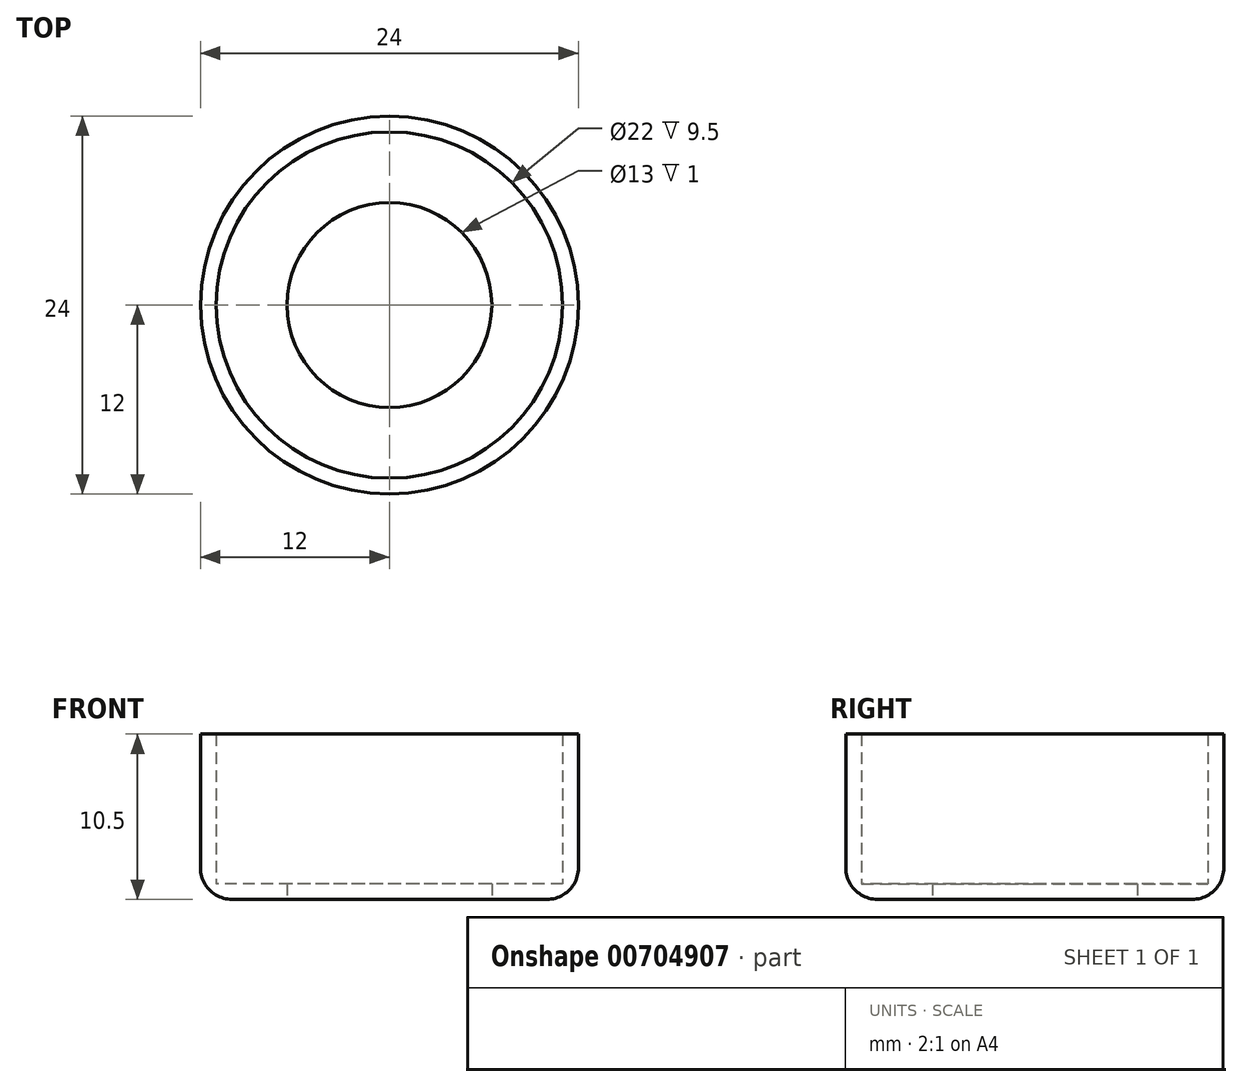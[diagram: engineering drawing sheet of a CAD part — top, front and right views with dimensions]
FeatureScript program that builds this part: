
annotation { "Feature Type Name" : "Feature", "Feature Type Description" : "" }
export const myFeature = defineFeature(function(context is Context, id is Id, definition is map)
    precondition{}
    {
        {
            var Q0;
            Q0=qCreatedBy(makeId("Top.planeOp"),FACE);
            var sketch = newSketch(context, id + "F0", { "sketchPlane" : qUnion([Q0])});
            skCircle(sketch, "E0", {"center": v(0, 0) * mm, "radius": 12 * mm});
            skCircle(sketch, "E1", {"center": v(0, 0) * mm, "radius": 11 * mm});
            skSolve(sketch);
        }
        {
            var Q0;
            Q0 = qSketchRegion(id + "F0", true);
            extrude(context, id + "F1", {"entities" : qUnion([Q0]), "depth" : 10.5 * mm, "offsetDistance" : 25 * mm});
        }
        {
            var Q0;
            Q0=makeQuery(id+"F0.imprint","IMPRINT",FACE,{"disambiguationData":[TD([[makeQuery(id+"F0.imprint","IMPRINT",EDGE,{"derivedFrom":sQuery(id+"F0.wireOp",EDGE,"E1")}),1.0]])]});
            extrude(context, id + "F2", {"entities" : qUnion([Q0]), "operationType" : NewBodyOperationType.ADD, "depth" : 1 * mm, "offsetDistance" : 25 * mm});
        }
        {
            var Q0;
            Q0=makeQuery(id+"F0.imprint","IMPRINT",FACE,{"disambiguationData":[TD([[makeQuery(id+"F0.imprint","IMPRINT",EDGE,{"derivedFrom":sQuery(id+"F0.wireOp",EDGE,"E1")}),1.0]])]});
            var sketch = newSketch(context, id + "F3", { "sketchPlane" : qUnion([Q0])});
            skCircle(sketch, "E2", {"center": v(0, 0) * mm, "radius": 6.5 * mm});
            skSolve(sketch);
        }
        {
            var Q0;
            Q0=makeQuery(id+"F3.imprint","IMPRINT",FACE,{"disambiguationData":[TD([[makeQuery(id+"F3.imprint","IMPRINT",EDGE,{"derivedFrom":sQuery(id+"F3.wireOp",EDGE,"E2")}),1.0]])]});
            extrude(context, id + "F4", {"entities" : qUnion([Q0]), "operationType" : NewBodyOperationType.REMOVE, "depth" : 25 * mm, "offsetDistance" : 25 * mm});
        }
        {
            var Q0;
            Q0=makeQuery(id+"F1.opExtrude","CAP_EDGE",EDGE,{"disambiguationData":[OSD([sQuery(id+"F0.wireOp",EDGE,"E0")])],"isStart":true});
            var Q1;
            Q1=makeQuery(id+"F4.boolean.opBoolean","COPY",EDGE,{"derivedFrom":makeQuery(id+"F4.opExtrude","CAP_EDGE",EDGE,{"disambiguationData":[OSD([sQuery(id+"F3.wireOp",EDGE,"E2")])],"isStart":true})});
            fillet(context, id + "F5", {"entities" : qUnion([Q0, Q1]), "radius" : 2 * mm, "tangentPropagation" : true, "allowEdgeOverflow" : false});
        }
    });
